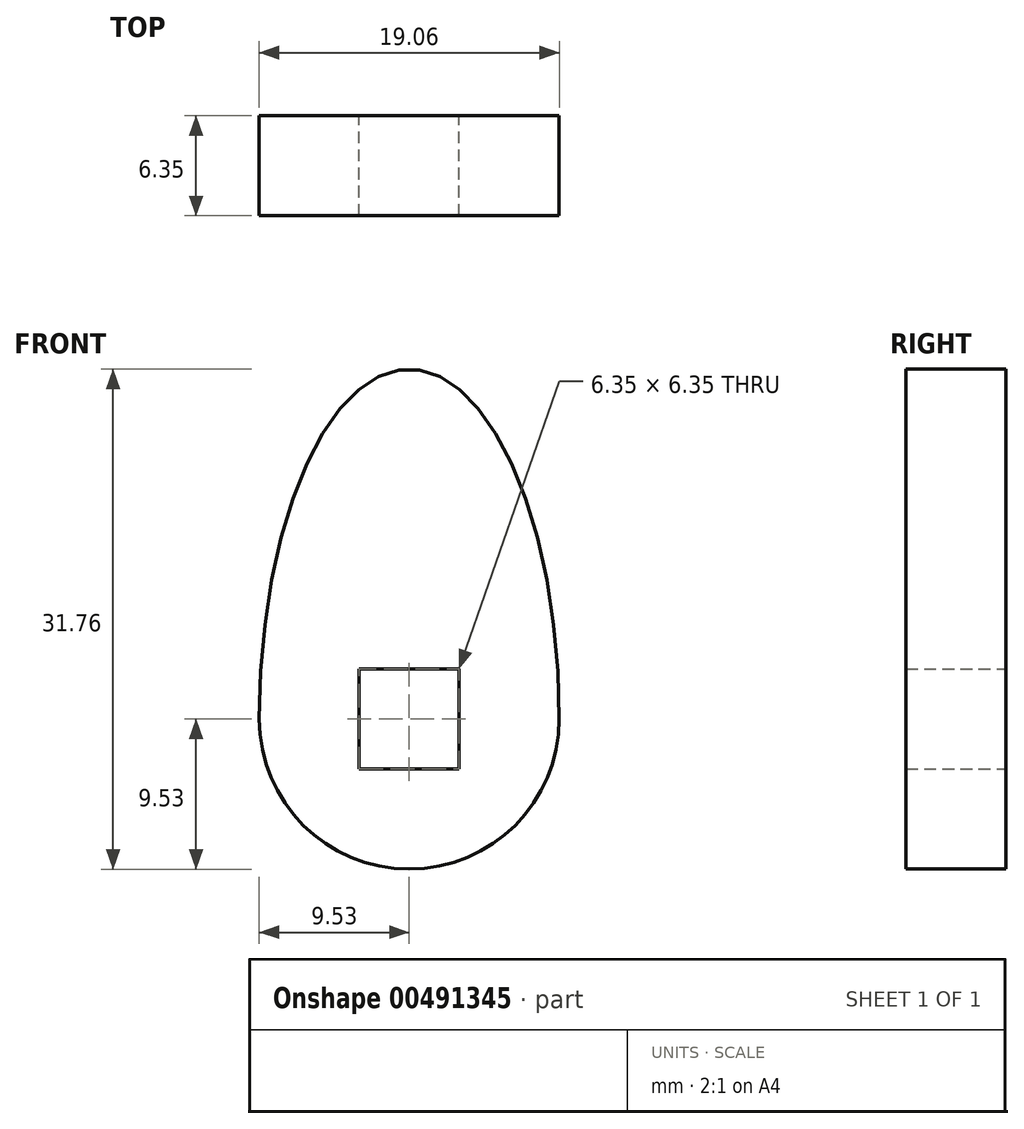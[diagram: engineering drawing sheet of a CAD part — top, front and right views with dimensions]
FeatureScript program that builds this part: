
annotation { "Feature Type Name" : "Feature", "Feature Type Description" : "" }
export const myFeature = defineFeature(function(context is Context, id is Id, definition is map)
    precondition{}
    {
        {
            var Q0;
            Q0=qCreatedBy(makeId("Front.planeOp"),FACE);
            var sketch = newSketch(context, id + "F0", { "sketchPlane" : qUnion([Q0])});
            skCircle(sketch, "E0", {"center": v(0, 0) * mm, "radius": 9.53 * mm});
            skEllipse(sketch, "E1", {"center": v(0, 0) * mm, "majorRadius": 22.23 * mm, "minorRadius": 9.53 * mm, "majorAxis": v(0, -1)});
            skPoint(sketch, "E2", {"position": v(0, -9.53) * mm});
            skPoint(sketch, "E3", {"position": v(0, 22.23) * mm});
            skLineSegment(sketch, "E4.bottom", {"start": v(3.18, 3.17) * mm, "end": v(-3.17, 3.17) * mm});
            skLineSegment(sketch, "E4.top", {"start": v(3.18, -3.18) * mm, "end": v(-3.18, -3.18) * mm});
            skLineSegment(sketch, "E4.left", {"start": v(3.18, 3.18) * mm, "end": v(3.18, -3.18) * mm});
            skLineSegment(sketch, "E4.right", {"start": v(-3.18, 3.18) * mm, "end": v(-3.18, -3.18) * mm});
            skSolve(sketch);
        }
        {
            var Q0;
            {var subQ0=sQuery(id+"F0.wireOp",EDGE,"E1");var subQ1=sQuery(id+"F0.wireOp",EDGE,"E0");var subQ2=makeQuery(id+"F0.imprint","INTERSECT",VERTEX,{"disambiguationData":[OD(0.0)],"derivedFrom":[subQ1,subQ0]});Q0=makeQuery(id+"F0.imprint","IMPRINT",FACE,{"disambiguationData":[TD([[makeQuery(id+"F0.imprint","IMPRINT",EDGE,{"disambiguationData":[TD([[subQ2,1.0]])],"derivedFrom":subQ1}),-1.0]])]});}
            var Q1;
            Q1=makeQuery(id+"F0.imprint","IMPRINT",FACE,{"disambiguationData":[TD([[makeQuery(id+"F0.imprint","IMPRINT",EDGE,{"derivedFrom":sQuery(id+"F0.wireOp",EDGE,"E4.bottom")}),-1.0]])]});
            extrude(context, id + "F1", {"entities" : qUnion([Q0, Q1]), "depth" : 6.35 * mm});
        }
    });
